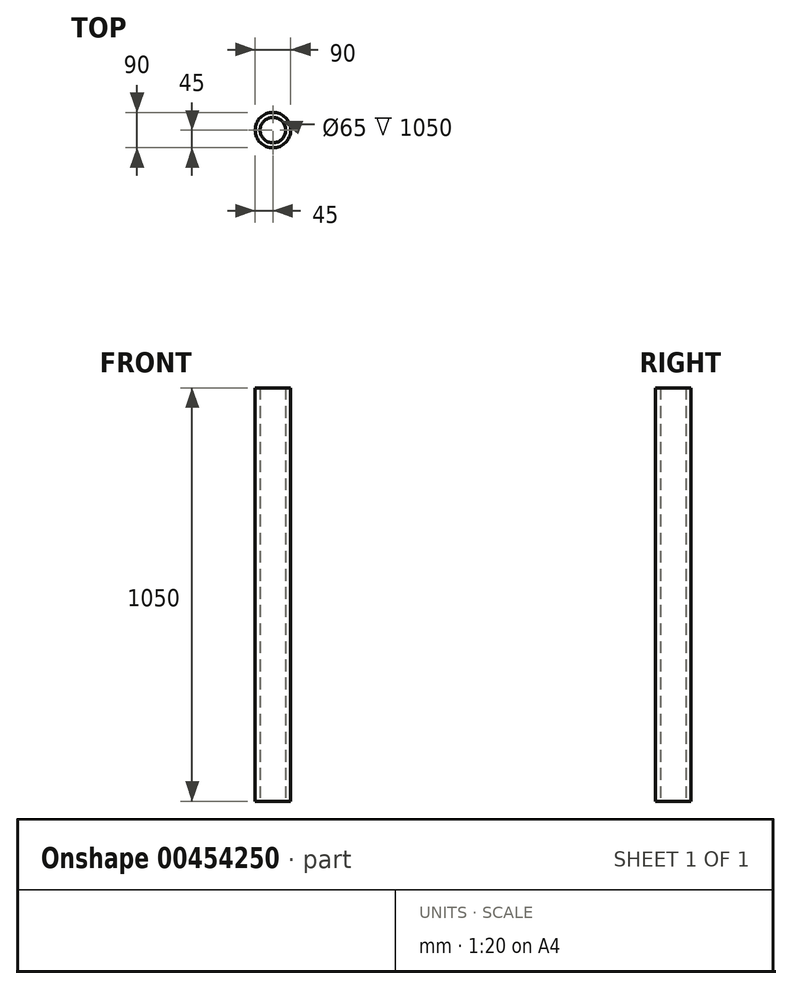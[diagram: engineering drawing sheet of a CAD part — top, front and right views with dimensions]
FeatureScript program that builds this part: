
annotation { "Feature Type Name" : "Feature", "Feature Type Description" : "" }
export const myFeature = defineFeature(function(context is Context, id is Id, definition is map)
    precondition{}
    {
        {
            var Q0;
            Q0=qCreatedBy(makeId("Top.planeOp"),FACE);
            var sketch = newSketch(context, id + "F0", { "sketchPlane" : qUnion([Q0])});
            skCircle(sketch, "E0", {"center": v(0, 0) * mm, "radius": 45 * mm});
            skCircle(sketch, "E1", {"center": v(0, 0) * mm, "radius": 32.5 * mm});
            skSolve(sketch);
        }
        {
            var Q0;
            Q0 = qSketchRegion(id + "F0", true);
            extrude(context, id + "F1", {"entities" : qUnion([Q0]), "depth" : 1050 * mm});
        }
        {
            var Q0;
            Q0 = qSketchRegion(id + "F0", true);
            var sketch = newSketch(context, id + "F2", { "sketchPlane" : qUnion([Q0])});
            skCircle(sketch, "E2", {"center": v(0, 0) * mm, "radius": 43 * mm});
            skCircle(sketch, "E3", {"center": v(0, 0) * mm, "radius": 32.5 * mm});
            skSolve(sketch);
        }
        {
            var Q0;
            Q0 = qSketchRegion(id + "F2", true);
            extrude(context, id + "F3", {"entities" : qUnion([Q0]), "operationType" : NewBodyOperationType.ADD, "depth" : 255 * mm});
        }
    });
